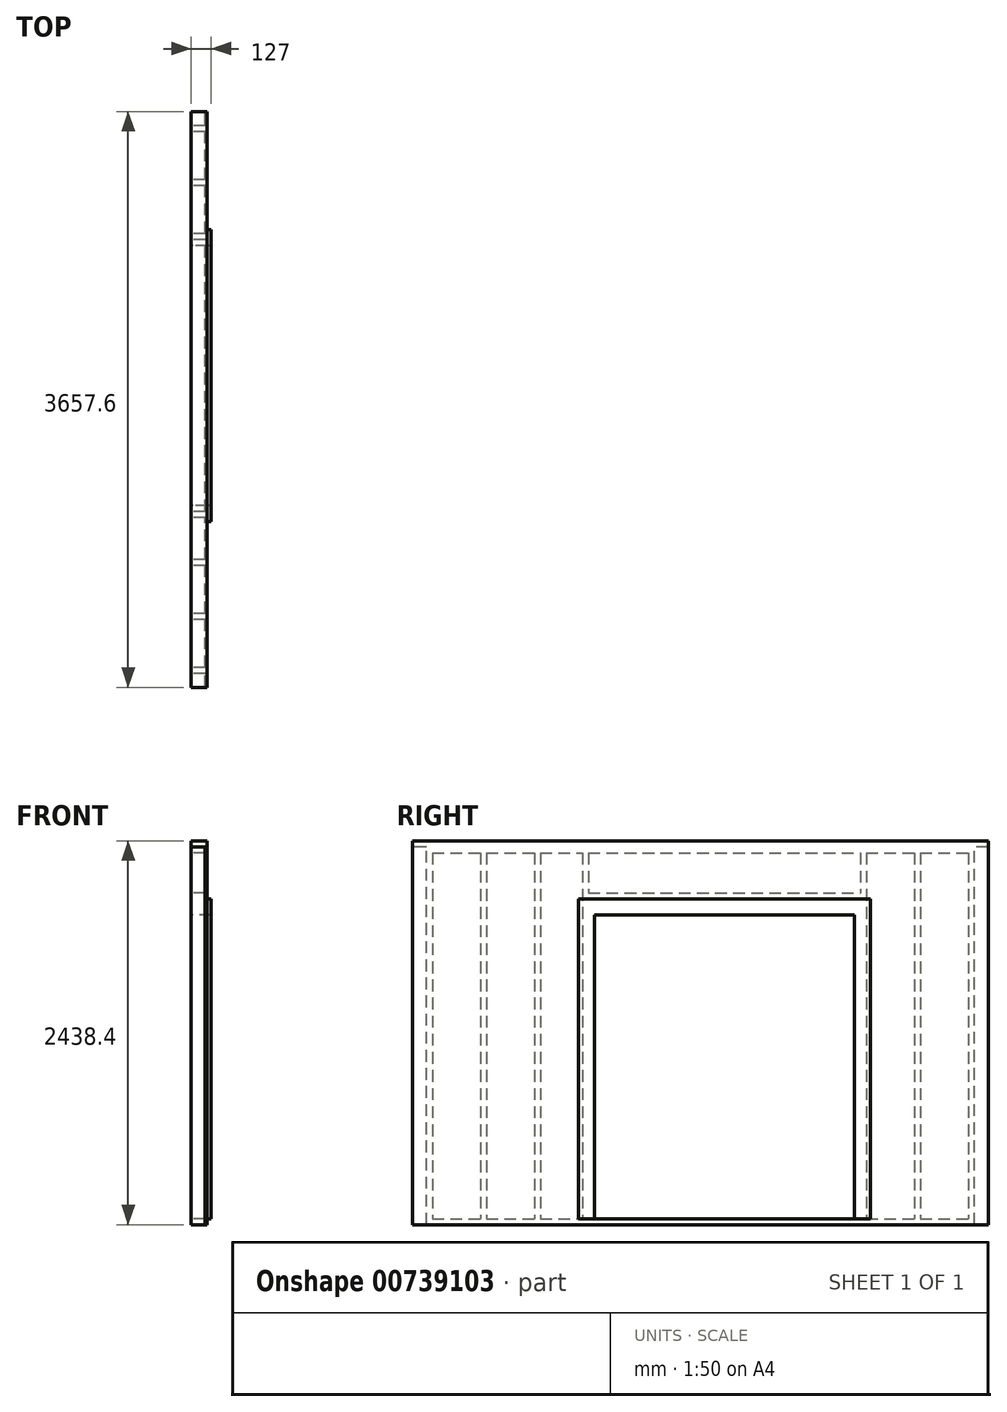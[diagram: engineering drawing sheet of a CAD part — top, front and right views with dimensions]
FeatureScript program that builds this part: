
annotation { "Feature Type Name" : "Feature", "Feature Type Description" : "" }
export const myFeature = defineFeature(function(context is Context, id is Id, definition is map)
    precondition{}
    {
        {
            var Q0;
            Q0=qCreatedBy(makeId("Right.planeOp"),FACE);
            var sketch = newSketch(context, id + "F0", { "sketchPlane" : qUnion([Q0])});
            skLineSegment(sketch, "E0.bottom", {"start": v(0, 0) * mm, "end": v(3479.8, 0) * mm});
            skLineSegment(sketch, "E0.top", {"start": v(0, 2400.3) * mm, "end": v(3479.8, 2400.3) * mm});
            skLineSegment(sketch, "E0.left", {"start": v(0, 0) * mm, "end": v(0, 2400.3) * mm});
            skLineSegment(sketch, "E0.right", {"start": v(3479.8, 0) * mm, "end": v(3479.8, 2400.3) * mm});
            skLineSegment(sketch, "E1", {"start": v(0, 38.1) * mm, "end": v(3479.8, 38.1) * mm});
            skLineSegment(sketch, "E2", {"start": v(0, 2362.2) * mm, "end": v(3479.8, 2362.2) * mm});
            skLineSegment(sketch, "E3", {"start": v(38.1, 2362.2) * mm, "end": v(38.1, 38.1) * mm});
            skLineSegment(sketch, "E4", {"start": v(3441.7, 2362.2) * mm, "end": v(3441.7, 38.1) * mm});
            skLineSegment(sketch, "E5", {"start": v(0, 2400.3) * mm, "end": v(-88.9, 2400.3) * mm});
            skLineSegment(sketch, "E6", {"start": v(-88.9, 2400.3) * mm, "end": v(-88.9, 2438.4) * mm});
            skLineSegment(sketch, "E7", {"start": v(-88.9, 2438.4) * mm, "end": v(3568.7, 2438.4) * mm});
            skLineSegment(sketch, "E8", {"start": v(3568.7, 2438.4) * mm, "end": v(3568.7, 2400.3) * mm});
            skLineSegment(sketch, "E9", {"start": v(3568.7, 2400.3) * mm, "end": v(3479.8, 2400.3) * mm});
            skLineSegment(sketch, "E10", {"start": v(342.9, 2362.2) * mm, "end": v(342.9, 38.1) * mm});
            skLineSegment(sketch, "E11", {"start": v(381, 2362.2) * mm, "end": v(381, 38.1) * mm});
            skLineSegment(sketch, "E12", {"start": v(990.6, 2362.2) * mm, "end": v(990.6, 38.1) * mm});
            skLineSegment(sketch, "E13", {"start": v(1028.7, 2362.2) * mm, "end": v(1028.7, 38.1) * mm});
            skLineSegment(sketch, "E14", {"start": v(1739.9, 2590.8) * mm, "end": v(1739.9, -360.45) * mm, "construction": true});
            skLineSegment(sketch, "E15.MirrorCS", {"start": v(2755.9, 2362.2) * mm, "end": v(2755.9, 38.1) * mm});
            skLineSegment(sketch, "E16.MirrorCS", {"start": v(2794, 2362.2) * mm, "end": v(2794, 38.1) * mm});
            skLineSegment(sketch, "E17", {"start": v(1028.7, 1968.5) * mm, "end": v(2755.9, 1968.5) * mm});
            skLineSegment(sketch, "E18", {"start": v(1028.7, 2108.2) * mm, "end": v(2755.9, 2108.2) * mm});
            skLineSegment(sketch, "E19", {"start": v(1066.8, 1968.5) * mm, "end": v(1066.8, 38.1) * mm});
            skLineSegment(sketch, "E20", {"start": v(2717.8, 1968.5) * mm, "end": v(2717.8, 38.1) * mm});
            skLineSegment(sketch, "E21", {"start": v(3098.8, 2362.2) * mm, "end": v(3098.8, 38.1) * mm});
            skLineSegment(sketch, "E22", {"start": v(3136.9, 2362.2) * mm, "end": v(3136.9, 38.1) * mm});
            skLineSegment(sketch, "E23", {"start": v(685.8, 2362.2) * mm, "end": v(685.8, 38.1) * mm});
            skLineSegment(sketch, "E24", {"start": v(723.9, 2362.2) * mm, "end": v(723.9, 38.1) * mm});
            skLineSegment(sketch, "E25", {"start": v(1130.3, 2722.62) * mm, "end": v(1130.3, -813) * mm, "construction": true});
            skLineSegment(sketch, "E26", {"start": v(2349.5, 2709.64) * mm, "end": v(2349.5, -341.6) * mm, "construction": true});
            skSolve(sketch);
        }
        {
            var Q0;
            {var subQ5=sQuery(id+"F0.wireOp",EDGE,"E3");Q0=makeQuery(id+"F0.imprint","IMPRINT",FACE,{"disambiguationData":[TD([[makeQuery(id+"F0.imprint","IMPRINT",EDGE,{"derivedFrom":subQ5}),-1.0]])]});}
            var Q1;
            {var subQ0=sQuery(id+"F0.wireOp",EDGE,"E10");Q1=makeQuery(id+"F0.imprint","IMPRINT",FACE,{"disambiguationData":[TD([[makeQuery(id+"F0.imprint","IMPRINT",EDGE,{"derivedFrom":subQ0}),1.0]])]});}
            var Q2;
            {var subQ0=sQuery(id+"F0.wireOp",EDGE,"E12");Q2=makeQuery(id+"F0.imprint","IMPRINT",FACE,{"disambiguationData":[TD([[makeQuery(id+"F0.imprint","IMPRINT",EDGE,{"derivedFrom":subQ0}),1.0]])]});}
            var Q3;
            {var subQ3=sQuery(id+"F0.wireOp",EDGE,"E19");Q3=makeQuery(id+"F0.imprint","IMPRINT",FACE,{"disambiguationData":[TD([[makeQuery(id+"F0.imprint","IMPRINT",EDGE,{"derivedFrom":subQ3}),-1.0]])]});}
            var Q4;
            {var subQ7=sQuery(id+"F0.wireOp",EDGE,"E18");Q4=makeQuery(id+"F0.imprint","IMPRINT",FACE,{"disambiguationData":[TD([[makeQuery(id+"F0.imprint","IMPRINT",EDGE,{"derivedFrom":subQ7}),-1.0]])]});}
            var Q5;
            {var subQ3=sQuery(id+"F0.wireOp",EDGE,"E20");Q5=makeQuery(id+"F0.imprint","IMPRINT",FACE,{"disambiguationData":[TD([[makeQuery(id+"F0.imprint","IMPRINT",EDGE,{"derivedFrom":subQ3}),1.0]])]});}
            var Q6;
            {var subQ5=sQuery(id+"F0.wireOp",EDGE,"E16.MirrorCS");Q6=makeQuery(id+"F0.imprint","IMPRINT",FACE,{"disambiguationData":[TD([[makeQuery(id+"F0.imprint","IMPRINT",EDGE,{"derivedFrom":subQ5}),-1.0]])]});}
            var Q7;
            {var subQ5=sQuery(id+"F0.wireOp",EDGE,"E4");Q7=makeQuery(id+"F0.imprint","IMPRINT",FACE,{"disambiguationData":[TD([[makeQuery(id+"F0.imprint","IMPRINT",EDGE,{"derivedFrom":subQ5}),1.0]])]});}
            var Q8;
            {var subQ0=sQuery(id+"F0.wireOp",EDGE,"ebc93e1c-2fd9-4a12-a1d5-9430a37e263e0.MirrorCS");Q8=makeQuery(id+"F0.imprint","IMPRINT",FACE,{"disambiguationData":[TD([[makeQuery(id+"F0.imprint","IMPRINT",EDGE,{"derivedFrom":subQ0}),1.0]])]});}
            var Q9;
            {var subQ4=sQuery(id+"F0.wireOp",EDGE,"E0.top");Q9=makeQuery(id+"F0.imprint","IMPRINT",FACE,{"disambiguationData":[TD([[makeQuery(id+"F0.imprint","IMPRINT",EDGE,{"derivedFrom":subQ4}),-1.0]])]});}
            var Q10;
            Q10=makeQuery(id+"F0.imprint","IMPRINT",FACE,{"disambiguationData":[TD([[makeQuery(id+"F0.imprint","IMPRINT",EDGE,{"derivedFrom":sQuery(id+"F0.wireOp",EDGE,"E0.top")}),1.0]])]});
            var Q11;
            {var subQ8=sQuery(id+"F0.wireOp",EDGE,"E0.bottom");Q11=makeQuery(id+"F0.imprint","IMPRINT",FACE,{"disambiguationData":[TD([[makeQuery(id+"F0.imprint","IMPRINT",EDGE,{"derivedFrom":subQ8}),1.0]])]});}
            var Q12;
            {var subQ0=sQuery(id+"F0.wireOp",EDGE,"E23");Q12=makeQuery(id+"F0.imprint","IMPRINT",FACE,{"disambiguationData":[TD([[makeQuery(id+"F0.imprint","IMPRINT",EDGE,{"derivedFrom":subQ0}),1.0]])]});}
            var Q13;
            {var subQ0=sQuery(id+"F0.wireOp",EDGE,"E21");Q13=makeQuery(id+"F0.imprint","IMPRINT",FACE,{"disambiguationData":[TD([[makeQuery(id+"F0.imprint","IMPRINT",EDGE,{"derivedFrom":subQ0}),1.0]])]});}
            extrude(context, id + "F1", {"entities" : qUnion([Q0, Q1, Q2, Q3, Q4, Q5, Q6, Q7, Q8, Q9, Q10, Q11, Q12, Q13]), "depth" : 88.9 * mm, "offsetDistance" : 25.4 * mm});
        }
        {
            var Q0;
            Q0=makeQuery(id+"F1.opExtrude","CAP_FACE",FACE,{"disambiguationData":[OSD([sQuery(id+"F0.wireOp",EDGE,"E0.bottom"),sQuery(id+"F0.wireOp",EDGE,"E0.left"),sQuery(id+"F0.wireOp",EDGE,"E0.right"),sQuery(id+"F0.wireOp",EDGE,"E1"),sQuery(id+"F0.wireOp",EDGE,"E2"),sQuery(id+"F0.wireOp",EDGE,"E3"),sQuery(id+"F0.wireOp",EDGE,"E4"),sQuery(id+"F0.wireOp",EDGE,"E5"),sQuery(id+"F0.wireOp",EDGE,"E6"),sQuery(id+"F0.wireOp",EDGE,"E7"),sQuery(id+"F0.wireOp",EDGE,"E8"),sQuery(id+"F0.wireOp",EDGE,"E9"),sQuery(id+"F0.wireOp",EDGE,"E10"),sQuery(id+"F0.wireOp",EDGE,"E11"),sQuery(id+"F0.wireOp",EDGE,"E12"),sQuery(id+"F0.wireOp",EDGE,"E13"),sQuery(id+"F0.wireOp",EDGE,"E15.MirrorCS"),sQuery(id+"F0.wireOp",EDGE,"E16.MirrorCS"),sQuery(id+"F0.wireOp",EDGE,"E17"),sQuery(id+"F0.wireOp",EDGE,"E18"),sQuery(id+"F0.wireOp",EDGE,"E19"),sQuery(id+"F0.wireOp",EDGE,"E20"),sQuery(id+"F0.wireOp",EDGE,"E21"),sQuery(id+"F0.wireOp",EDGE,"E22"),sQuery(id+"F0.wireOp",EDGE,"E23"),sQuery(id+"F0.wireOp",EDGE,"E24")])],"isStart":false});
            var sketch = newSketch(context, id + "F2", { "sketchPlane" : qUnion([Q0])});
            skLineSegment(sketch, "E27.0", {"start": v(-88.9, 2438.4) * mm, "end": v(3568.7, 2438.4) * mm});
            skLineSegment(sketch, "E28", {"start": v(-88.9, 2438.4) * mm, "end": v(-88.9, 0) * mm});
            skLineSegment(sketch, "E29", {"start": v(-88.9, 0) * mm, "end": v(3568.7, 0) * mm});
            skLineSegment(sketch, "E30", {"start": v(3568.7, 0) * mm, "end": v(3568.7, 2438.4) * mm});
            skLineSegment(sketch, "E31.0", {"start": v(1066.8, 1968.5) * mm, "end": v(1066.8, 38.1) * mm});
            skLineSegment(sketch, "E31.1", {"start": v(1066.8, 1968.5) * mm, "end": v(2717.8, 1968.5) * mm});
            skLineSegment(sketch, "E31.2", {"start": v(2717.8, 1968.5) * mm, "end": v(2717.8, 38.1) * mm});
            skLineSegment(sketch, "E31.3", {"start": v(1066.8, 38.1) * mm, "end": v(2717.8, 38.1) * mm});
            skSolve(sketch);
        }
        {
            var Q0;
            Q0 = qSketchRegion(id + "F2", true);
            extrude(context, id + "F3", {"entities" : qUnion([Q0]), "operationType" : NewBodyOperationType.ADD, "depth" : 12.7 * mm, "offsetDistance" : 25.4 * mm});
        }
        {
            var Q0;
            Q0=makeQuery(id+"F3.opExtrude","CAP_FACE",FACE,{"disambiguationData":[OSD([sQuery(id+"F2.wireOp",EDGE,"E27.0"),sQuery(id+"F2.wireOp",EDGE,"E28"),sQuery(id+"F2.wireOp",EDGE,"E29"),sQuery(id+"F2.wireOp",EDGE,"E30"),sQuery(id+"F2.wireOp",EDGE,"E31.0"),sQuery(id+"F2.wireOp",EDGE,"E31.1"),sQuery(id+"F2.wireOp",EDGE,"E31.2"),sQuery(id+"F2.wireOp",EDGE,"E31.3")])],"isStart":false});
            var sketch = newSketch(context, id + "F4", { "sketchPlane" : qUnion([Q0])});
            skLineSegment(sketch, "E32.0", {"start": v(1066.8, 1968.5) * mm, "end": v(1066.8, 38.1) * mm});
            skLineSegment(sketch, "E32.1", {"start": v(1066.8, 1968.5) * mm, "end": v(2717.8, 1968.5) * mm});
            skLineSegment(sketch, "E32.2", {"start": v(2717.8, 1968.5) * mm, "end": v(2717.8, 38.1) * mm});
            skLineSegment(sketch, "E33.0", {"start": v(965.2, 2070.1) * mm, "end": v(965.2, 38.1) * mm});
            skLineSegment(sketch, "E33.1", {"start": v(965.2, 2070.1) * mm, "end": v(2819.4, 2070.1) * mm});
            skLineSegment(sketch, "E33.2", {"start": v(2819.4, 2070.1) * mm, "end": v(2819.4, 38.1) * mm});
            skLineSegment(sketch, "E34", {"start": v(965.2, 38.1) * mm, "end": v(1066.8, 38.1) * mm});
            skLineSegment(sketch, "E35", {"start": v(2717.8, 38.1) * mm, "end": v(2819.4, 38.1) * mm});
            skSolve(sketch);
        }
        {
            var Q0;
            Q0 = qSketchRegion(id + "F4", true);
            extrude(context, id + "F5", {"entities" : qUnion([Q0]), "operationType" : NewBodyOperationType.ADD, "depth" : 25.4 * mm, "offsetDistance" : 25.4 * mm});
        }
    });
